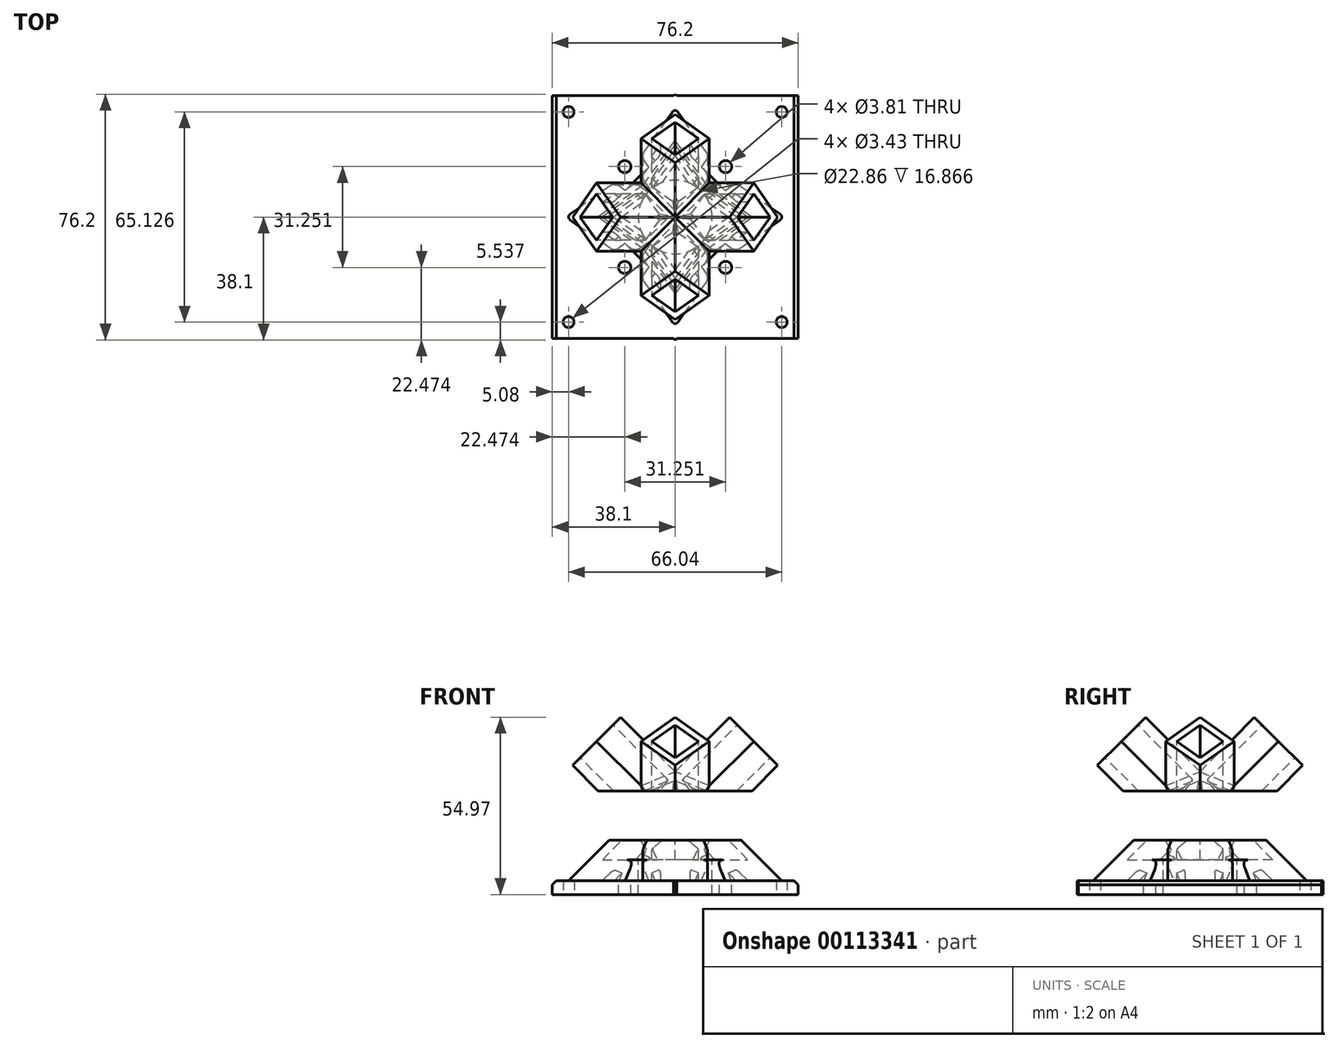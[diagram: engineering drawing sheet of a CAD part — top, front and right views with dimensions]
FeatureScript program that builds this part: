
annotation { "Feature Type Name" : "Feature", "Feature Type Description" : "" }
export const myFeature = defineFeature(function(context is Context, id is Id, definition is map)
    precondition{}
    {
        {
            var Q0;
            Q0=qCreatedBy(makeId("Top.planeOp"),FACE);
            var sketch = newSketch(context, id + "F0", { "sketchPlane" : qUnion([Q0])});
            skLineSegment(sketch, "E0", {"start": v(0, 0) * mm, "end": v(0, 35.93) * mm, "construction": true});
            skLineSegment(sketch, "E1", {"start": v(0, 0) * mm, "end": v(30.29, 0) * mm, "construction": true});
            skLineSegment(sketch, "E2", {"start": v(0, 0) * mm, "end": v(34.43, 34.43) * mm, "construction": true});
            skLineSegment(sketch, "E3", {"start": v(0, 38.1) * mm, "end": v(38.1, 0) * mm});
            skLineSegment(sketch, "E4", {"start": v(38.1, 0) * mm, "end": v(0, -38.1) * mm});
            skLineSegment(sketch, "E5", {"start": v(0, -38.1) * mm, "end": v(-38.1, 0) * mm});
            skLineSegment(sketch, "E6", {"start": v(-38.1, 0) * mm, "end": v(0, 38.1) * mm});
            skSolve(sketch);
        }
        {
            var Q0;
            Q0=qSketchRegion(id+"F0",true);
            extrude(context, id + "F1", {"entities" : qUnion([Q0]), "depth" : 4.32 * mm});
        }
        {
            var Q0;
            Q0=sQuery(id+"F0.wireOp",EDGE,"E1");
            var Q1;
            Q1=qCreatedBy(makeId("Top.planeOp"),FACE);
            cPlane(context, id + "F2", {"entities" : qUnion([Q0, Q1]), "cplaneType" : CPlaneType.LINE_ANGLE, "offset" : 25.4 * mm, "angle" : 45 * degree, "width" : 152.4 * mm, "height" : 152.4 * mm});
        }
        {
            var Q0;
            Q0=qCreatedBy(id+"F2.planeOp",FACE);
            cPlane(context, id + "F3", {"entities" : qUnion([Q0]), "cplaneType" : CPlaneType.OFFSET, "offset" : 50.8 * mm, "oppositeDirection" : true, "width" : 152.4 * mm, "height" : 152.4 * mm});
        }
        {
            var Q0;
            Q0=qCreatedBy(makeId("Right.planeOp"),FACE);
            var sketch = newSketch(context, id + "F4", { "sketchPlane" : qUnion([Q0])});
            skLineSegment(sketch, "E7", {"start": v(0, 0) * mm, "end": v(0, 27.83) * mm, "construction": true});
            skLineSegment(sketch, "E8", {"start": v(-38.1, 0) * mm, "end": v(-56.06, 17.96) * mm, "construction": true});
            skSolve(sketch);
        }
        {
            var Q0;
            Q0=qCreatedBy(id+"F3.planeOp",FACE);
            var sketch = newSketch(context, id + "F5", { "sketchPlane" : qUnion([Q0])});
            skLineSegment(sketch, "E9", {"start": v(0, 26.94) * mm, "end": v(-10.56, 16.38) * mm});
            skLineSegment(sketch, "E10", {"start": v(0, 26.94) * mm, "end": v(0, 0) * mm, "construction": true});
            skLineSegment(sketch, "E11", {"start": v(-10.56, 16.38) * mm, "end": v(0, 5.82) * mm});
            skLineSegment(sketch, "E12", {"start": v(0, 26.94) * mm, "end": v(10.56, 16.38) * mm});
            skLineSegment(sketch, "E13", {"start": v(10.56, 16.38) * mm, "end": v(0, 5.82) * mm});
            skLineSegment(sketch, "E14", {"start": v(0, 23.56) * mm, "end": v(7.18, 16.38) * mm});
            skLineSegment(sketch, "E15", {"start": v(7.18, 16.38) * mm, "end": v(0, 9.2) * mm});
            skLineSegment(sketch, "E16", {"start": v(0, 9.2) * mm, "end": v(-7.18, 16.38) * mm});
            skLineSegment(sketch, "E17", {"start": v(-7.18, 16.38) * mm, "end": v(0, 23.56) * mm});
            skSolve(sketch);
        }
        {
            var Q0;
            Q0=makeQuery(id+"F5.imprint","IMPRINT",FACE,{"disambiguationData":[TD([[makeQuery(id+"F5.imprint","IMPRINT",EDGE,{"derivedFrom":sQuery(id+"F5.wireOp",EDGE,"E9")}),1.0]])]});
            extrude(context, id + "F6", {"entities" : qUnion([Q0]), "operationType" : NewBodyOperationType.ADD, "endBound" : BoundingType.UP_TO_NEXT, "depth" : 25.4 * mm});
        }
        {
            var Q0;
            Q0=makeQuery(id+"F6.opExtrude","SWEPT_FACE",FACE,{"disambiguationData":[OSD([sQuery(id+"F5.wireOp",EDGE,"E11")])]});
            cPlane(context, id + "F7", {"entities" : qUnion([Q0]), "cplaneType" : CPlaneType.OFFSET, "offset" : 0 * mm, "width" : 152.4 * mm, "height" : 152.4 * mm});
        }
        {
            var Q0;
            Q0=qCreatedBy(id+"F7.planeOp",FACE);
            var sketch = newSketch(context, id + "F8", { "sketchPlane" : qUnion([Q0])});
            skLineSegment(sketch, "E18", {"start": v(30.54, 7.4) * mm, "end": v(48.17, 19.87) * mm, "construction": true});
            skCircle(sketch, "E19.cCircle", {"center": v(30.54, 7.4) * mm, "radius": 1.65 * mm, "construction": true});
            skLineSegment(sketch, "E19.0", {"start": v(32.27, 6.6) * mm, "end": v(30.71, 5.5) * mm});
            skLineSegment(sketch, "E19.1", {"start": v(30.71, 5.5) * mm, "end": v(28.98, 6.3) * mm});
            skLineSegment(sketch, "E19.2", {"start": v(28.98, 6.3) * mm, "end": v(28.8, 8.2) * mm});
            skLineSegment(sketch, "E19.3", {"start": v(28.8, 8.2) * mm, "end": v(30.36, 9.3) * mm});
            skLineSegment(sketch, "E19.4", {"start": v(30.36, 9.3) * mm, "end": v(32.1, 8.5) * mm});
            skLineSegment(sketch, "E19.5", {"start": v(32.1, 8.5) * mm, "end": v(32.27, 6.6) * mm});
            skPoint(sketch, "E19.0.midPoint", {"position": v(31.5, 6.06) * mm});
            skSolve(sketch);
        }
        {
            var Q0;
            Q0=qSketchRegion(id+"F8",true);
            extrude(context, id + "F9", {"entities" : qUnion([Q0]), "operationType" : NewBodyOperationType.REMOVE, "oppositeDirection" : true, "depth" : 2.54 * mm});
        }
        {
            var Q0;
            Q0=makeQuery(id+"F1.opExtrude","SWEPT_BODY",BODY,{"disambiguationData":[OSD([sQuery(id+"F0.wireOp",EDGE,"E3"),sQuery(id+"F0.wireOp",EDGE,"E4"),sQuery(id+"F0.wireOp",EDGE,"E5"),sQuery(id+"F0.wireOp",EDGE,"E6")])]});
            var Q1;
            Q1=sQuery(id+"F4.wireOp",EDGE,"E7");
            circularPattern(context, id + "F10", {"entities" : qUnion([Q0]), "axis" : qUnion([Q1]), "angle" : 90 * degree, "instanceCount" : 4});
        }
        {
            var Q0;
            Q0=qCreatedBy(makeId("Top.planeOp"),FACE);
            cPlane(context, id + "F11", {"entities" : qUnion([Q0]), "cplaneType" : CPlaneType.OFFSET, "offset" : 25.4 * mm, "width" : 152.4 * mm, "height" : 152.4 * mm});
        }
        {
            var Q0;
            Q0=qCreatedBy(id+"F11.planeOp",FACE);
            var sketch = newSketch(context, id + "F12", { "sketchPlane" : qUnion([Q0])});
            skCircle(sketch, "E20", {"center": v(0, 0) * mm, "radius": 11.43 * mm});
            skSolve(sketch);
        }
        {
            var Q0;
            Q0=qCreatedBy(makeId("Top.planeOp"),FACE);
            var sketch = newSketch(context, id + "F13", { "sketchPlane" : qUnion([Q0])});
            skLineSegment(sketch, "E21.bottom", {"start": v(19.05, 19.05) * mm, "end": v(-19.05, 19.05) * mm});
            skLineSegment(sketch, "E21.top", {"start": v(19.05, -19.05) * mm, "end": v(-19.05, -19.05) * mm});
            skLineSegment(sketch, "E21.left", {"start": v(19.05, 19.05) * mm, "end": v(19.05, -19.05) * mm});
            skLineSegment(sketch, "E21.right", {"start": v(-19.05, 19.05) * mm, "end": v(-19.05, -19.05) * mm});
            skPoint(sketch, "E21.middle", {"position": v(0, 0) * mm});
            skLineSegment(sketch, "E22", {"start": v(-19.05, 4.6) * mm, "end": v(-4.6, 19.05) * mm});
            skLineSegment(sketch, "E23", {"start": v(-19.05, -4.6) * mm, "end": v(-4.6, -19.05) * mm});
            skLineSegment(sketch, "E24", {"start": v(4.6, 19.05) * mm, "end": v(19.05, 4.6) * mm});
            skLineSegment(sketch, "E25", {"start": v(4.6, -19.05) * mm, "end": v(19.05, -4.6) * mm});
            skSolve(sketch);
        }
        {
            var Q0;
            {var subQ3=sQuery(id+"F13.wireOp",EDGE,"E22");Q0=makeQuery(id+"F13.imprint","IMPRINT",FACE,{"disambiguationData":[TD([[makeQuery(id+"F13.imprint","IMPRINT",EDGE,{"derivedFrom":subQ3}),-1.0]])]});}
            extrude(context, id + "F14", {"entities" : qUnion([Q0]), "depth" : 10.8 * mm});
        }
        {
            var Q0;
            Q0=qCreatedBy(id+"F11.planeOp",FACE);
            var sketch = newSketch(context, id + "F15", { "sketchPlane" : qUnion([Q0])});
            skCircle(sketch, "E26", {"center": v(0, 0) * mm, "radius": 22.1 * mm, "construction": true});
            skLineSegment(sketch, "E27", {"start": v(0, 0) * mm, "end": v(0, 32.05) * mm, "construction": true});
            skLineSegment(sketch, "E28", {"start": v(0, 0) * mm, "end": v(26.77, 26.77) * mm, "construction": true});
            skCircle(sketch, "E29", {"center": v(15.63, 15.63) * mm, "radius": 1.9 * mm});
            skCircle(sketch, "E30.1.0", {"center": v(-15.63, 15.63) * mm, "radius": 1.9 * mm});
            skCircle(sketch, "E30.2.0", {"center": v(-15.63, -15.63) * mm, "radius": 1.9 * mm});
            skCircle(sketch, "E30.3.0", {"center": v(15.63, -15.63) * mm, "radius": 1.9 * mm});
            skLineSegment(sketch, "E31", {"start": v(0, 0) * mm, "end": v(-26.06, 26.06) * mm, "construction": true});
            skSolve(sketch);
        }
        {
            var Q0;
            Q0=makeQuery(id+"F10.opPattern","COPY",BODY,{"derivedFrom":makeQuery(id+"F1.opExtrude","SWEPT_BODY",BODY,{"disambiguationData":[OSD([sQuery(id+"F0.wireOp",EDGE,"E3"),sQuery(id+"F0.wireOp",EDGE,"E4"),sQuery(id+"F0.wireOp",EDGE,"E5"),sQuery(id+"F0.wireOp",EDGE,"E6")])]}),"instanceName":"2"});
            var Q1;
            Q1=makeQuery(id+"F14.opExtrude","SWEPT_BODY",BODY,{"disambiguationData":[OSD([sQuery(id+"F13.wireOp",EDGE,"E21.bottom"),sQuery(id+"F13.wireOp",EDGE,"E21.top"),sQuery(id+"F13.wireOp",EDGE,"E21.left"),sQuery(id+"F13.wireOp",EDGE,"E21.right"),sQuery(id+"F13.wireOp",EDGE,"E22"),sQuery(id+"F13.wireOp",EDGE,"E23"),sQuery(id+"F13.wireOp",EDGE,"E24"),sQuery(id+"F13.wireOp",EDGE,"E25")])]});
            booleanBodies(context, id + "F16", {"operationType" : BooleanOperationType.UNION, "tools" : qUnion([Q0, Q1])});
        }
        {
            var Q0;
            Q0=makeQuery(id+"F10.opPattern","COPY",BODY,{"derivedFrom":makeQuery(id+"F1.opExtrude","SWEPT_BODY",BODY,{"disambiguationData":[OSD([sQuery(id+"F0.wireOp",EDGE,"E3"),sQuery(id+"F0.wireOp",EDGE,"E4"),sQuery(id+"F0.wireOp",EDGE,"E5"),sQuery(id+"F0.wireOp",EDGE,"E6")])]}),"instanceName":"2"});
            var Q1;
            Q1=makeQuery(id+"F10.opPattern","COPY",BODY,{"derivedFrom":makeQuery(id+"F1.opExtrude","SWEPT_BODY",BODY,{"disambiguationData":[OSD([sQuery(id+"F0.wireOp",EDGE,"E3"),sQuery(id+"F0.wireOp",EDGE,"E4"),sQuery(id+"F0.wireOp",EDGE,"E5"),sQuery(id+"F0.wireOp",EDGE,"E6")])]}),"instanceName":"3"});
            var Q2;
            Q2=makeQuery(id+"F1.opExtrude","SWEPT_BODY",BODY,{"disambiguationData":[OSD([sQuery(id+"F0.wireOp",EDGE,"E3"),sQuery(id+"F0.wireOp",EDGE,"E4"),sQuery(id+"F0.wireOp",EDGE,"E5"),sQuery(id+"F0.wireOp",EDGE,"E6")])]});
            var Q3;
            Q3=makeQuery(id+"F10.opPattern","COPY",BODY,{"derivedFrom":makeQuery(id+"F1.opExtrude","SWEPT_BODY",BODY,{"disambiguationData":[OSD([sQuery(id+"F0.wireOp",EDGE,"E3"),sQuery(id+"F0.wireOp",EDGE,"E4"),sQuery(id+"F0.wireOp",EDGE,"E5"),sQuery(id+"F0.wireOp",EDGE,"E6")])]}),"instanceName":"1"});
            booleanBodies(context, id + "F17", {"operationType" : BooleanOperationType.UNION, "tools" : qUnion([Q0, Q1, Q2, Q3])});
        }
        {
            var Q0;
            {var subQ4=makeQuery(id+"F6.opExtrude","SWEPT_FACE",FACE,{"disambiguationData":[OSD([sQuery(id+"F5.wireOp",EDGE,"E11")])]});var subQ6=sQuery(id+"F13.wireOp",EDGE,"E21.right");Q0=makeQuery(id+"F17.opBoolean","SPLIT",FACE,{"disambiguationData":[TD([makeQuery(id+"F10.opPattern","COPY",FACE,{"derivedFrom":subQ4,"instanceName":"3"})])],"derivedFrom":makeQuery(id+"F14.opExtrude","SWEPT_FACE",FACE,{"disambiguationData":[OSD([subQ6])]})});}
            var Q1;
            {var subQ4=makeQuery(id+"F6.opExtrude","SWEPT_FACE",FACE,{"disambiguationData":[OSD([sQuery(id+"F5.wireOp",EDGE,"E13")])]});var subQ6=sQuery(id+"F13.wireOp",EDGE,"E21.right");Q1=makeQuery(id+"F17.opBoolean","SPLIT",FACE,{"disambiguationData":[TD([makeQuery(id+"F10.opPattern","COPY",FACE,{"derivedFrom":subQ4,"instanceName":"3"})])],"derivedFrom":makeQuery(id+"F14.opExtrude","SWEPT_FACE",FACE,{"disambiguationData":[OSD([subQ6])]})});}
            extrude(context, id + "F18", {"entities" : qUnion([Q0, Q1]), "operationType" : NewBodyOperationType.ADD, "endBound" : BoundingType.UP_TO_NEXT, "depth" : 25.4 * mm});
        }
        {
            var Q0;
            {var subQ0=makeQuery(id+"F6.opExtrude","SWEPT_FACE",FACE,{"disambiguationData":[OSD([sQuery(id+"F5.wireOp",EDGE,"E13")])]});var subQ6=sQuery(id+"F13.wireOp",EDGE,"E21.bottom");Q0=makeQuery(id+"F16.opBoolean","SPLIT",FACE,{"disambiguationData":[TD([makeQuery(id+"F10.opPattern","COPY",FACE,{"derivedFrom":subQ0,"instanceName":"2"})])],"derivedFrom":makeQuery(id+"F14.opExtrude","SWEPT_FACE",FACE,{"disambiguationData":[OSD([subQ6])]})});}
            var Q1;
            {var subQ4=makeQuery(id+"F6.opExtrude","SWEPT_FACE",FACE,{"disambiguationData":[OSD([sQuery(id+"F5.wireOp",EDGE,"E11")])]});var subQ6=sQuery(id+"F13.wireOp",EDGE,"E21.bottom");Q1=makeQuery(id+"F16.opBoolean","SPLIT",FACE,{"disambiguationData":[TD([makeQuery(id+"F10.opPattern","COPY",FACE,{"derivedFrom":subQ4,"instanceName":"2"})])],"derivedFrom":makeQuery(id+"F14.opExtrude","SWEPT_FACE",FACE,{"disambiguationData":[OSD([subQ6])]})});}
            extrude(context, id + "F19", {"entities" : qUnion([Q0, Q1]), "operationType" : NewBodyOperationType.ADD, "endBound" : BoundingType.UP_TO_NEXT, "depth" : 25.4 * mm});
        }
        {
            var Q0;
            {var subQ0=makeQuery(id+"F6.opExtrude","SWEPT_FACE",FACE,{"disambiguationData":[OSD([sQuery(id+"F5.wireOp",EDGE,"E11")])]});var subQ6=sQuery(id+"F13.wireOp",EDGE,"E21.left");Q0=makeQuery(id+"F17.opBoolean","SPLIT",FACE,{"disambiguationData":[TD([makeQuery(id+"F10.opPattern","COPY",FACE,{"derivedFrom":subQ0,"instanceName":"1"})])],"derivedFrom":makeQuery(id+"F14.opExtrude","SWEPT_FACE",FACE,{"disambiguationData":[OSD([subQ6])]})});}
            var Q1;
            {var subQ0=makeQuery(id+"F6.opExtrude","SWEPT_FACE",FACE,{"disambiguationData":[OSD([sQuery(id+"F5.wireOp",EDGE,"E13")])]});var subQ6=sQuery(id+"F13.wireOp",EDGE,"E21.left");Q1=makeQuery(id+"F17.opBoolean","SPLIT",FACE,{"disambiguationData":[TD([makeQuery(id+"F10.opPattern","COPY",FACE,{"derivedFrom":subQ0,"instanceName":"1"})])],"derivedFrom":makeQuery(id+"F14.opExtrude","SWEPT_FACE",FACE,{"disambiguationData":[OSD([subQ6])]})});}
            extrude(context, id + "F20", {"entities" : qUnion([Q0, Q1]), "operationType" : NewBodyOperationType.ADD, "endBound" : BoundingType.UP_TO_NEXT, "depth" : 25.4 * mm});
        }
        {
            var Q0;
            {var subQ0=makeQuery(id+"F6.opExtrude","SWEPT_FACE",FACE,{"disambiguationData":[OSD([sQuery(id+"F5.wireOp",EDGE,"E13")])]});var subQ2=sQuery(id+"F13.wireOp",EDGE,"E21.top");Q0=makeQuery(id+"F17.opBoolean","SPLIT",FACE,{"disambiguationData":[TD([subQ0])],"derivedFrom":makeQuery(id+"F14.opExtrude","SWEPT_FACE",FACE,{"disambiguationData":[OSD([subQ2])]})});}
            var Q1;
            {var subQ0=makeQuery(id+"F6.opExtrude","SWEPT_FACE",FACE,{"disambiguationData":[OSD([sQuery(id+"F5.wireOp",EDGE,"E11")])]});var subQ6=sQuery(id+"F13.wireOp",EDGE,"E21.top");Q1=makeQuery(id+"F17.opBoolean","SPLIT",FACE,{"disambiguationData":[TD([subQ0])],"derivedFrom":makeQuery(id+"F14.opExtrude","SWEPT_FACE",FACE,{"disambiguationData":[OSD([subQ6])]})});}
            extrude(context, id + "F21", {"entities" : qUnion([Q0, Q1]), "operationType" : NewBodyOperationType.ADD, "endBound" : BoundingType.UP_TO_NEXT, "depth" : 25.4 * mm});
        }
        {
            var Q0;
            Q0=qCreatedBy(makeId("Right.planeOp"),FACE);
            cPlane(context, id + "F22", {"entities" : qUnion([Q0]), "cplaneType" : CPlaneType.OFFSET, "offset" : 63.5 * mm, "width" : 152.4 * mm, "height" : 152.4 * mm});
        }
        {
            var Q0;
            Q0=qCreatedBy(id+"F22.planeOp",FACE);
            var sketch = newSketch(context, id + "F23", { "sketchPlane" : qUnion([Q0])});
            skLineSegment(sketch, "E32.bottom", {"start": v(-55.88, 16.87) * mm, "end": v(55.88, 16.87) * mm});
            skLineSegment(sketch, "E32.top", {"start": v(-55.88, 32.1) * mm, "end": v(55.88, 32.1) * mm});
            skLineSegment(sketch, "E32.left", {"start": v(-55.88, 16.87) * mm, "end": v(-55.88, 32.1) * mm});
            skLineSegment(sketch, "E32.right", {"start": v(55.88, 16.87) * mm, "end": v(55.88, 32.1) * mm});
            skSolve(sketch);
        }
        {
            var Q0;
            Q0=qSketchRegion(id+"F23",true);
            extrude(context, id + "F24", {"entities" : qUnion([Q0]), "operationType" : NewBodyOperationType.REMOVE, "oppositeDirection" : true, "depth" : 152.4 * mm});
        }
        {
            var Q0;
            Q0=makeQuery(id+"F10.opPattern","COPY",EDGE,{"derivedFrom":makeQuery(id+"F6.opExtrude","SWEPT_EDGE",EDGE,{"disambiguationData":[OSD([sQuery(id+"F5.wireOp",EDGE,"E11"),sQuery(id+"F5.wireOp",EDGE,"E13")])]}),"instanceName":"2"});
            var Q1;
            Q1=makeQuery(id+"F10.opPattern","COPY",EDGE,{"derivedFrom":makeQuery(id+"F6.opExtrude","SWEPT_EDGE",EDGE,{"disambiguationData":[OSD([sQuery(id+"F5.wireOp",EDGE,"E9"),sQuery(id+"F5.wireOp",EDGE,"E11")])]}),"instanceName":"2"});
            var Q2;
            Q2=makeQuery(id+"F10.opPattern","COPY",EDGE,{"derivedFrom":makeQuery(id+"F6.opExtrude","SWEPT_EDGE",EDGE,{"disambiguationData":[OSD([sQuery(id+"F5.wireOp",EDGE,"E9"),sQuery(id+"F5.wireOp",EDGE,"E12")])]}),"instanceName":"2"});
            var Q3;
            Q3=makeQuery(id+"F10.opPattern","COPY",EDGE,{"derivedFrom":makeQuery(id+"F6.opExtrude","SWEPT_EDGE",EDGE,{"disambiguationData":[OSD([sQuery(id+"F5.wireOp",EDGE,"E12"),sQuery(id+"F5.wireOp",EDGE,"E13")])]}),"instanceName":"2"});
            var Q4;
            Q4=makeQuery(id+"F10.opPattern","COPY",EDGE,{"derivedFrom":makeQuery(id+"F6.opExtrude","SWEPT_EDGE",EDGE,{"disambiguationData":[OSD([sQuery(id+"F5.wireOp",EDGE,"E12"),sQuery(id+"F5.wireOp",EDGE,"E13")])]}),"instanceName":"1"});
            var Q5;
            Q5=makeQuery(id+"F10.opPattern","COPY",EDGE,{"derivedFrom":makeQuery(id+"F6.opExtrude","SWEPT_EDGE",EDGE,{"disambiguationData":[OSD([sQuery(id+"F5.wireOp",EDGE,"E9"),sQuery(id+"F5.wireOp",EDGE,"E12")])]}),"instanceName":"1"});
            var Q6;
            Q6=makeQuery(id+"F10.opPattern","COPY",EDGE,{"derivedFrom":makeQuery(id+"F6.opExtrude","SWEPT_EDGE",EDGE,{"disambiguationData":[OSD([sQuery(id+"F5.wireOp",EDGE,"E9"),sQuery(id+"F5.wireOp",EDGE,"E11")])]}),"instanceName":"1"});
            var Q7;
            Q7=makeQuery(id+"F10.opPattern","COPY",EDGE,{"derivedFrom":makeQuery(id+"F6.opExtrude","SWEPT_EDGE",EDGE,{"disambiguationData":[OSD([sQuery(id+"F5.wireOp",EDGE,"E11"),sQuery(id+"F5.wireOp",EDGE,"E13")])]}),"instanceName":"1"});
            fillet(context, id + "F25", {"entities" : qUnion([Q0, Q1, Q2, Q3, Q4, Q5, Q6, Q7]), "radius" : 1.27 * mm, "tangentPropagation" : true, "allowEdgeOverflow" : false});
        }
        {
            var Q0;
            Q0=makeQuery(id+"F6.opExtrude","SWEPT_EDGE",EDGE,{"disambiguationData":[OSD([sQuery(id+"F5.wireOp",EDGE,"E9"),sQuery(id+"F5.wireOp",EDGE,"E11")])]});
            var Q1;
            Q1=makeQuery(id+"F6.opExtrude","SWEPT_EDGE",EDGE,{"disambiguationData":[OSD([sQuery(id+"F5.wireOp",EDGE,"E9"),sQuery(id+"F5.wireOp",EDGE,"E12")])]});
            var Q2;
            Q2=makeQuery(id+"F6.opExtrude","SWEPT_EDGE",EDGE,{"disambiguationData":[OSD([sQuery(id+"F5.wireOp",EDGE,"E12"),sQuery(id+"F5.wireOp",EDGE,"E13")])]});
            var Q3;
            Q3=makeQuery(id+"F6.opExtrude","SWEPT_EDGE",EDGE,{"disambiguationData":[OSD([sQuery(id+"F5.wireOp",EDGE,"E11"),sQuery(id+"F5.wireOp",EDGE,"E13")])]});
            var Q4;
            Q4=makeQuery(id+"F10.opPattern","COPY",EDGE,{"derivedFrom":makeQuery(id+"F6.opExtrude","SWEPT_EDGE",EDGE,{"disambiguationData":[OSD([sQuery(id+"F5.wireOp",EDGE,"E11"),sQuery(id+"F5.wireOp",EDGE,"E13")])]}),"instanceName":"3"});
            var Q5;
            Q5=makeQuery(id+"F10.opPattern","COPY",EDGE,{"derivedFrom":makeQuery(id+"F6.opExtrude","SWEPT_EDGE",EDGE,{"disambiguationData":[OSD([sQuery(id+"F5.wireOp",EDGE,"E12"),sQuery(id+"F5.wireOp",EDGE,"E13")])]}),"instanceName":"3"});
            var Q6;
            Q6=makeQuery(id+"F10.opPattern","COPY",EDGE,{"derivedFrom":makeQuery(id+"F6.opExtrude","SWEPT_EDGE",EDGE,{"disambiguationData":[OSD([sQuery(id+"F5.wireOp",EDGE,"E9"),sQuery(id+"F5.wireOp",EDGE,"E11")])]}),"instanceName":"3"});
            var Q7;
            Q7=makeQuery(id+"F10.opPattern","COPY",EDGE,{"derivedFrom":makeQuery(id+"F6.opExtrude","SWEPT_EDGE",EDGE,{"disambiguationData":[OSD([sQuery(id+"F5.wireOp",EDGE,"E9"),sQuery(id+"F5.wireOp",EDGE,"E12")])]}),"instanceName":"3"});
            fillet(context, id + "F26", {"entities" : qUnion([Q0, Q1, Q2, Q3, Q4, Q5, Q6, Q7]), "radius" : 1.27 * mm, "tangentPropagation" : true, "allowEdgeOverflow" : false});
        }
        {
            var Q0;
            Q0=makeQuery(id+"F20.opExtrude","TWEAK_EDGE",EDGE,{"derivedFrom":[makeQuery(id+"F14.opExtrude","SWEPT_EDGE",EDGE,{"disambiguationData":[OSD([sQuery(id+"F13.wireOp",EDGE,"E21.left"),sQuery(id+"F13.wireOp",EDGE,"E24")])]}),makeQuery(id+"F10.opPattern","COPY",FACE,{"derivedFrom":makeQuery(id+"F6.opExtrude","SWEPT_FACE",FACE,{"disambiguationData":[OSD([sQuery(id+"F5.wireOp",EDGE,"E13")])]}),"instanceName":"1"})]});
            var Q1;
            {var subQ0=sQuery(id+"F13.wireOp",EDGE,"E24");var subQ1=sQuery(id+"F13.wireOp",EDGE,"E21.left");Q1=makeQuery(id+"F20.boolean.opBoolean","MERGE",EDGE,{"derivedFrom":[makeQuery(id+"F14.opExtrude","SWEPT_EDGE",EDGE,{"disambiguationData":[OSD([subQ1,subQ0])]}),makeQuery(id+"F20.opExtrude","CAP_EDGE",EDGE,{"disambiguationData":[OSD([subQ1,subQ0])],"isStart":true})]});}
            var Q2;
            {var subQ0=sQuery(id+"F13.wireOp",EDGE,"E24");var subQ1=sQuery(id+"F13.wireOp",EDGE,"E21.bottom");Q2=makeQuery(id+"F19.boolean.opBoolean","MERGE",EDGE,{"derivedFrom":[makeQuery(id+"F14.opExtrude","SWEPT_EDGE",EDGE,{"disambiguationData":[OSD([subQ1,subQ0])]}),makeQuery(id+"F19.opExtrude","CAP_EDGE",EDGE,{"disambiguationData":[OSD([subQ1,subQ0])],"isStart":true})]});}
            var Q3;
            Q3=makeQuery(id+"F19.opExtrude","TWEAK_EDGE",EDGE,{"derivedFrom":[makeQuery(id+"F14.opExtrude","SWEPT_EDGE",EDGE,{"disambiguationData":[OSD([sQuery(id+"F13.wireOp",EDGE,"E21.bottom"),sQuery(id+"F13.wireOp",EDGE,"E24")])]}),makeQuery(id+"F10.opPattern","COPY",FACE,{"derivedFrom":makeQuery(id+"F6.opExtrude","SWEPT_FACE",FACE,{"disambiguationData":[OSD([sQuery(id+"F5.wireOp",EDGE,"E11")])]}),"instanceName":"2"})]});
            var Q4;
            Q4=makeQuery(id+"F19.opExtrude","TWEAK_EDGE",EDGE,{"derivedFrom":[makeQuery(id+"F14.opExtrude","SWEPT_EDGE",EDGE,{"disambiguationData":[OSD([sQuery(id+"F13.wireOp",EDGE,"E21.bottom"),sQuery(id+"F13.wireOp",EDGE,"E22")])]}),makeQuery(id+"F10.opPattern","COPY",FACE,{"derivedFrom":makeQuery(id+"F6.opExtrude","SWEPT_FACE",FACE,{"disambiguationData":[OSD([sQuery(id+"F5.wireOp",EDGE,"E13")])]}),"instanceName":"2"})]});
            var Q5;
            {var subQ0=sQuery(id+"F13.wireOp",EDGE,"E22");var subQ1=sQuery(id+"F13.wireOp",EDGE,"E21.bottom");Q5=makeQuery(id+"F19.boolean.opBoolean","MERGE",EDGE,{"derivedFrom":[makeQuery(id+"F14.opExtrude","SWEPT_EDGE",EDGE,{"disambiguationData":[OSD([subQ1,subQ0])]}),makeQuery(id+"F19.opExtrude","CAP_EDGE",EDGE,{"disambiguationData":[OSD([subQ1,subQ0])],"isStart":true})]});}
            var Q6;
            {var subQ0=sQuery(id+"F13.wireOp",EDGE,"E22");var subQ1=sQuery(id+"F13.wireOp",EDGE,"E21.right");Q6=makeQuery(id+"F18.boolean.opBoolean","MERGE",EDGE,{"derivedFrom":[makeQuery(id+"F14.opExtrude","SWEPT_EDGE",EDGE,{"disambiguationData":[OSD([subQ1,subQ0])]}),makeQuery(id+"F18.opExtrude","CAP_EDGE",EDGE,{"disambiguationData":[OSD([subQ1,subQ0])],"isStart":true})]});}
            var Q7;
            Q7=makeQuery(id+"F18.opExtrude","TWEAK_EDGE",EDGE,{"derivedFrom":[makeQuery(id+"F14.opExtrude","SWEPT_EDGE",EDGE,{"disambiguationData":[OSD([sQuery(id+"F13.wireOp",EDGE,"E21.right"),sQuery(id+"F13.wireOp",EDGE,"E22")])]}),makeQuery(id+"F10.opPattern","COPY",FACE,{"derivedFrom":makeQuery(id+"F6.opExtrude","SWEPT_FACE",FACE,{"disambiguationData":[OSD([sQuery(id+"F5.wireOp",EDGE,"E11")])]}),"instanceName":"3"})]});
            var Q8;
            Q8=makeQuery(id+"F18.opExtrude","TWEAK_EDGE",EDGE,{"derivedFrom":[makeQuery(id+"F14.opExtrude","SWEPT_EDGE",EDGE,{"disambiguationData":[OSD([sQuery(id+"F13.wireOp",EDGE,"E21.right"),sQuery(id+"F13.wireOp",EDGE,"E23")])]}),makeQuery(id+"F10.opPattern","COPY",FACE,{"derivedFrom":makeQuery(id+"F6.opExtrude","SWEPT_FACE",FACE,{"disambiguationData":[OSD([sQuery(id+"F5.wireOp",EDGE,"E13")])]}),"instanceName":"3"})]});
            var Q9;
            {var subQ0=sQuery(id+"F13.wireOp",EDGE,"E23");var subQ1=sQuery(id+"F13.wireOp",EDGE,"E21.right");Q9=makeQuery(id+"F18.boolean.opBoolean","MERGE",EDGE,{"derivedFrom":[makeQuery(id+"F14.opExtrude","SWEPT_EDGE",EDGE,{"disambiguationData":[OSD([subQ1,subQ0])]}),makeQuery(id+"F18.opExtrude","CAP_EDGE",EDGE,{"disambiguationData":[OSD([subQ1,subQ0])],"isStart":true})]});}
            var Q10;
            {var subQ0=sQuery(id+"F13.wireOp",EDGE,"E23");var subQ1=sQuery(id+"F13.wireOp",EDGE,"E21.top");Q10=makeQuery(id+"F21.boolean.opBoolean","MERGE",EDGE,{"derivedFrom":[makeQuery(id+"F14.opExtrude","SWEPT_EDGE",EDGE,{"disambiguationData":[OSD([subQ1,subQ0])]}),makeQuery(id+"F21.opExtrude","CAP_EDGE",EDGE,{"disambiguationData":[OSD([subQ1,subQ0])],"isStart":true})]});}
            var Q11;
            Q11=makeQuery(id+"F21.opExtrude","TWEAK_EDGE",EDGE,{"derivedFrom":[makeQuery(id+"F14.opExtrude","SWEPT_EDGE",EDGE,{"disambiguationData":[OSD([sQuery(id+"F13.wireOp",EDGE,"E21.top"),sQuery(id+"F13.wireOp",EDGE,"E23")])]}),makeQuery(id+"F6.opExtrude","SWEPT_FACE",FACE,{"disambiguationData":[OSD([sQuery(id+"F5.wireOp",EDGE,"E11")])]})]});
            var Q12;
            Q12=makeQuery(id+"F21.opExtrude","TWEAK_EDGE",EDGE,{"derivedFrom":[makeQuery(id+"F14.opExtrude","SWEPT_EDGE",EDGE,{"disambiguationData":[OSD([sQuery(id+"F13.wireOp",EDGE,"E21.top"),sQuery(id+"F13.wireOp",EDGE,"E25")])]}),makeQuery(id+"F6.opExtrude","SWEPT_FACE",FACE,{"disambiguationData":[OSD([sQuery(id+"F5.wireOp",EDGE,"E13")])]})]});
            var Q13;
            {var subQ0=sQuery(id+"F13.wireOp",EDGE,"E25");var subQ1=sQuery(id+"F13.wireOp",EDGE,"E21.top");Q13=makeQuery(id+"F21.boolean.opBoolean","MERGE",EDGE,{"derivedFrom":[makeQuery(id+"F14.opExtrude","SWEPT_EDGE",EDGE,{"disambiguationData":[OSD([subQ1,subQ0])]}),makeQuery(id+"F21.opExtrude","CAP_EDGE",EDGE,{"disambiguationData":[OSD([subQ1,subQ0])],"isStart":true})]});}
            var Q14;
            {var subQ0=sQuery(id+"F13.wireOp",EDGE,"E25");var subQ1=sQuery(id+"F13.wireOp",EDGE,"E21.left");Q14=makeQuery(id+"F20.boolean.opBoolean","MERGE",EDGE,{"derivedFrom":[makeQuery(id+"F14.opExtrude","SWEPT_EDGE",EDGE,{"disambiguationData":[OSD([subQ1,subQ0])]}),makeQuery(id+"F20.opExtrude","CAP_EDGE",EDGE,{"disambiguationData":[OSD([subQ1,subQ0])],"isStart":true})]});}
            var Q15;
            Q15=makeQuery(id+"F20.opExtrude","TWEAK_EDGE",EDGE,{"derivedFrom":[makeQuery(id+"F14.opExtrude","SWEPT_EDGE",EDGE,{"disambiguationData":[OSD([sQuery(id+"F13.wireOp",EDGE,"E21.left"),sQuery(id+"F13.wireOp",EDGE,"E25")])]}),makeQuery(id+"F10.opPattern","COPY",FACE,{"derivedFrom":makeQuery(id+"F6.opExtrude","SWEPT_FACE",FACE,{"disambiguationData":[OSD([sQuery(id+"F5.wireOp",EDGE,"E11")])]}),"instanceName":"1"})]});
            fillet(context, id + "F27", {"entities" : qUnion([Q0, Q1, Q2, Q3, Q4, Q5, Q6, Q7, Q8, Q9, Q10, Q11, Q12, Q13, Q14, Q15]), "radius" : 2.54 * mm, "tangentPropagation" : true, "allowEdgeOverflow" : false});
        }
        {
            var Q0;
            Q0=qCreatedBy(makeId("Top.planeOp"),FACE);
            var sketch = newSketch(context, id + "F28", { "sketchPlane" : qUnion([Q0])});
            skLineSegment(sketch, "E33.bottom", {"start": v(38.1, 37.64) * mm, "end": v(-38.1, 37.64) * mm});
            skLineSegment(sketch, "E33.top", {"start": v(38.1, -37.64) * mm, "end": v(-38.1, -37.64) * mm});
            skLineSegment(sketch, "E33.left", {"start": v(38.1, 37.64) * mm, "end": v(38.1, -37.64) * mm});
            skLineSegment(sketch, "E33.right", {"start": v(-38.1, 37.64) * mm, "end": v(-38.1, -37.64) * mm});
            skPoint(sketch, "E33.middle", {"position": v(0, 0) * mm});
            skSolve(sketch);
        }
        {
            var Q0;
            Q0 = qSketchRegion(id + "F28", true);
            extrude(context, id + "F29", {"entities" : qUnion([Q0]), "operationType" : NewBodyOperationType.ADD, "depth" : 4.32 * mm});
        }
        {
            var Q0;
            Q0=makeQuery(id+"F15.imprint","IMPRINT",FACE,{"disambiguationData":[TD([[makeQuery(id+"F15.imprint","IMPRINT",EDGE,{"derivedFrom":sQuery(id+"F15.wireOp",EDGE,"E30.1.0")}),1.0]])]});
            var Q1;
            Q1=makeQuery(id+"F15.imprint","IMPRINT",FACE,{"disambiguationData":[TD([[makeQuery(id+"F15.imprint","IMPRINT",EDGE,{"derivedFrom":sQuery(id+"F15.wireOp",EDGE,"E29")}),1.0]])]});
            var Q2;
            Q2=makeQuery(id+"F15.imprint","IMPRINT",FACE,{"disambiguationData":[TD([[makeQuery(id+"F15.imprint","IMPRINT",EDGE,{"derivedFrom":sQuery(id+"F15.wireOp",EDGE,"E30.3.0")}),1.0]])]});
            var Q3;
            Q3=makeQuery(id+"F15.imprint","IMPRINT",FACE,{"disambiguationData":[TD([[makeQuery(id+"F15.imprint","IMPRINT",EDGE,{"derivedFrom":sQuery(id+"F15.wireOp",EDGE,"E30.2.0")}),1.0]])]});
            extrude(context, id + "F30", {"entities" : qUnion([Q0, Q1, Q2, Q3]), "operationType" : NewBodyOperationType.REMOVE, "oppositeDirection" : true, "depth" : 25.4 * mm});
        }
        {
            var Q0;
            Q0=qSketchRegion(id+"F12",true);
            extrude(context, id + "F31", {"entities" : qUnion([Q0]), "operationType" : NewBodyOperationType.REMOVE, "oppositeDirection" : true, "depth" : 25.4 * mm});
        }
        {
            var Q0;
            Q0=qCreatedBy(makeId("Top.planeOp"),FACE);
            var sketch = newSketch(context, id + "F32", { "sketchPlane" : qUnion([Q0])});
            skCircle(sketch, "E34", {"center": v(-33.02, -32.56) * mm, "radius": 1.71 * mm});
            skCircle(sketch, "E35", {"center": v(33.02, -32.56) * mm, "radius": 1.71 * mm});
            skCircle(sketch, "E36", {"center": v(33.02, 32.56) * mm, "radius": 1.71 * mm});
            skCircle(sketch, "E37", {"center": v(-33.02, 32.56) * mm, "radius": 1.71 * mm});
            skSolve(sketch);
        }
        {
            var Q0;
            Q0=makeQuery(id+"F32.imprint","IMPRINT",FACE,{"disambiguationData":[TD([[makeQuery(id+"F32.imprint","IMPRINT",EDGE,{"derivedFrom":sQuery(id+"F32.wireOp",EDGE,"E34")}),1.0]])]});
            var Q1;
            Q1=makeQuery(id+"F32.imprint","IMPRINT",FACE,{"disambiguationData":[TD([[makeQuery(id+"F32.imprint","IMPRINT",EDGE,{"derivedFrom":sQuery(id+"F32.wireOp",EDGE,"E35")}),1.0]])]});
            var Q2;
            Q2=makeQuery(id+"F32.imprint","IMPRINT",FACE,{"disambiguationData":[TD([[makeQuery(id+"F32.imprint","IMPRINT",EDGE,{"derivedFrom":sQuery(id+"F32.wireOp",EDGE,"E36")}),1.0]])]});
            var Q3;
            Q3=makeQuery(id+"F32.imprint","IMPRINT",FACE,{"disambiguationData":[TD([[makeQuery(id+"F32.imprint","IMPRINT",EDGE,{"derivedFrom":sQuery(id+"F32.wireOp",EDGE,"E37")}),1.0]])]});
            extrude(context, id + "F33", {"entities" : qUnion([Q0, Q1, Q2, Q3]), "operationType" : NewBodyOperationType.REMOVE, "depth" : 4.32 * mm});
        }
        {
            var Q0;
            {var subQ0=sQuery(id+"F28.wireOp",EDGE,"E33.top");var subQ5=makeQuery(id+"F6.opExtrude","SWEPT_FACE",FACE,{"disambiguationData":[OSD([sQuery(id+"F5.wireOp",EDGE,"E12")])]});Q0=makeQuery(id+"F29.boolean.opBoolean","SPLIT",EDGE,{"disambiguationData":[TD([subQ5])],"derivedFrom":makeQuery(id+"F29.opExtrude","CAP_EDGE",EDGE,{"disambiguationData":[OSD([subQ0])],"isStart":false})});}
            var Q1;
            {var subQ4=makeQuery(id+"F6.opExtrude","SWEPT_FACE",FACE,{"disambiguationData":[OSD([sQuery(id+"F5.wireOp",EDGE,"E9")])]});var subQ6=sQuery(id+"F28.wireOp",EDGE,"E33.left");Q1=makeQuery(id+"F29.boolean.opBoolean","SPLIT",EDGE,{"disambiguationData":[TD([makeQuery(id+"F10.opPattern","COPY",FACE,{"derivedFrom":subQ4,"instanceName":"1"})])],"derivedFrom":makeQuery(id+"F29.opExtrude","CAP_EDGE",EDGE,{"disambiguationData":[OSD([subQ6])],"isStart":false})});}
            var Q2;
            {var subQ1=makeQuery(id+"F6.opExtrude","SWEPT_FACE",FACE,{"disambiguationData":[OSD([sQuery(id+"F5.wireOp",EDGE,"E12")])]});var subQ6=sQuery(id+"F28.wireOp",EDGE,"E33.left");Q2=makeQuery(id+"F29.boolean.opBoolean","SPLIT",EDGE,{"disambiguationData":[TD([makeQuery(id+"F10.opPattern","COPY",FACE,{"derivedFrom":subQ1,"instanceName":"1"})])],"derivedFrom":makeQuery(id+"F29.opExtrude","CAP_EDGE",EDGE,{"disambiguationData":[OSD([subQ6])],"isStart":false})});}
            var Q3;
            {var subQ1=sQuery(id+"F28.wireOp",EDGE,"E33.bottom");var subQ6=makeQuery(id+"F6.opExtrude","SWEPT_FACE",FACE,{"disambiguationData":[OSD([sQuery(id+"F5.wireOp",EDGE,"E9")])]});Q3=makeQuery(id+"F29.boolean.opBoolean","SPLIT",EDGE,{"disambiguationData":[TD([makeQuery(id+"F10.opPattern","COPY",FACE,{"derivedFrom":subQ6,"instanceName":"2"})])],"derivedFrom":makeQuery(id+"F29.opExtrude","CAP_EDGE",EDGE,{"disambiguationData":[OSD([subQ1])],"isStart":false})});}
            var Q4;
            {var subQ1=sQuery(id+"F28.wireOp",EDGE,"E33.bottom");var subQ2=makeQuery(id+"F6.opExtrude","SWEPT_FACE",FACE,{"disambiguationData":[OSD([sQuery(id+"F5.wireOp",EDGE,"E12")])]});Q4=makeQuery(id+"F29.boolean.opBoolean","SPLIT",EDGE,{"disambiguationData":[TD([makeQuery(id+"F10.opPattern","COPY",FACE,{"derivedFrom":subQ2,"instanceName":"2"})])],"derivedFrom":makeQuery(id+"F29.opExtrude","CAP_EDGE",EDGE,{"disambiguationData":[OSD([subQ1])],"isStart":false})});}
            var Q5;
            {var subQ0=sQuery(id+"F28.wireOp",EDGE,"E33.right");var subQ2=makeQuery(id+"F6.opExtrude","SWEPT_FACE",FACE,{"disambiguationData":[OSD([sQuery(id+"F5.wireOp",EDGE,"E9")])]});Q5=makeQuery(id+"F29.boolean.opBoolean","SPLIT",EDGE,{"disambiguationData":[TD([makeQuery(id+"F10.opPattern","COPY",FACE,{"derivedFrom":subQ2,"instanceName":"3"})])],"derivedFrom":makeQuery(id+"F29.opExtrude","CAP_EDGE",EDGE,{"disambiguationData":[OSD([subQ0])],"isStart":false})});}
            var Q6;
            {var subQ1=makeQuery(id+"F6.opExtrude","SWEPT_FACE",FACE,{"disambiguationData":[OSD([sQuery(id+"F5.wireOp",EDGE,"E12")])]});var subQ6=sQuery(id+"F28.wireOp",EDGE,"E33.right");Q6=makeQuery(id+"F29.boolean.opBoolean","SPLIT",EDGE,{"disambiguationData":[TD([makeQuery(id+"F10.opPattern","COPY",FACE,{"derivedFrom":subQ1,"instanceName":"3"})])],"derivedFrom":makeQuery(id+"F29.opExtrude","CAP_EDGE",EDGE,{"disambiguationData":[OSD([subQ6])],"isStart":false})});}
            var Q7;
            {var subQ0=sQuery(id+"F28.wireOp",EDGE,"E33.top");var subQ5=makeQuery(id+"F6.opExtrude","SWEPT_FACE",FACE,{"disambiguationData":[OSD([sQuery(id+"F5.wireOp",EDGE,"E9")])]});Q7=makeQuery(id+"F29.boolean.opBoolean","SPLIT",EDGE,{"disambiguationData":[TD([subQ5])],"derivedFrom":makeQuery(id+"F29.opExtrude","CAP_EDGE",EDGE,{"disambiguationData":[OSD([subQ0])],"isStart":false})});}
            chamfer(context, id + "F34", {"entities" : qUnion([Q0, Q1, Q2, Q3, Q4, Q5, Q6, Q7]), "width" : 1.27 * mm, "tangentPropagation" : true});
        }
    });
